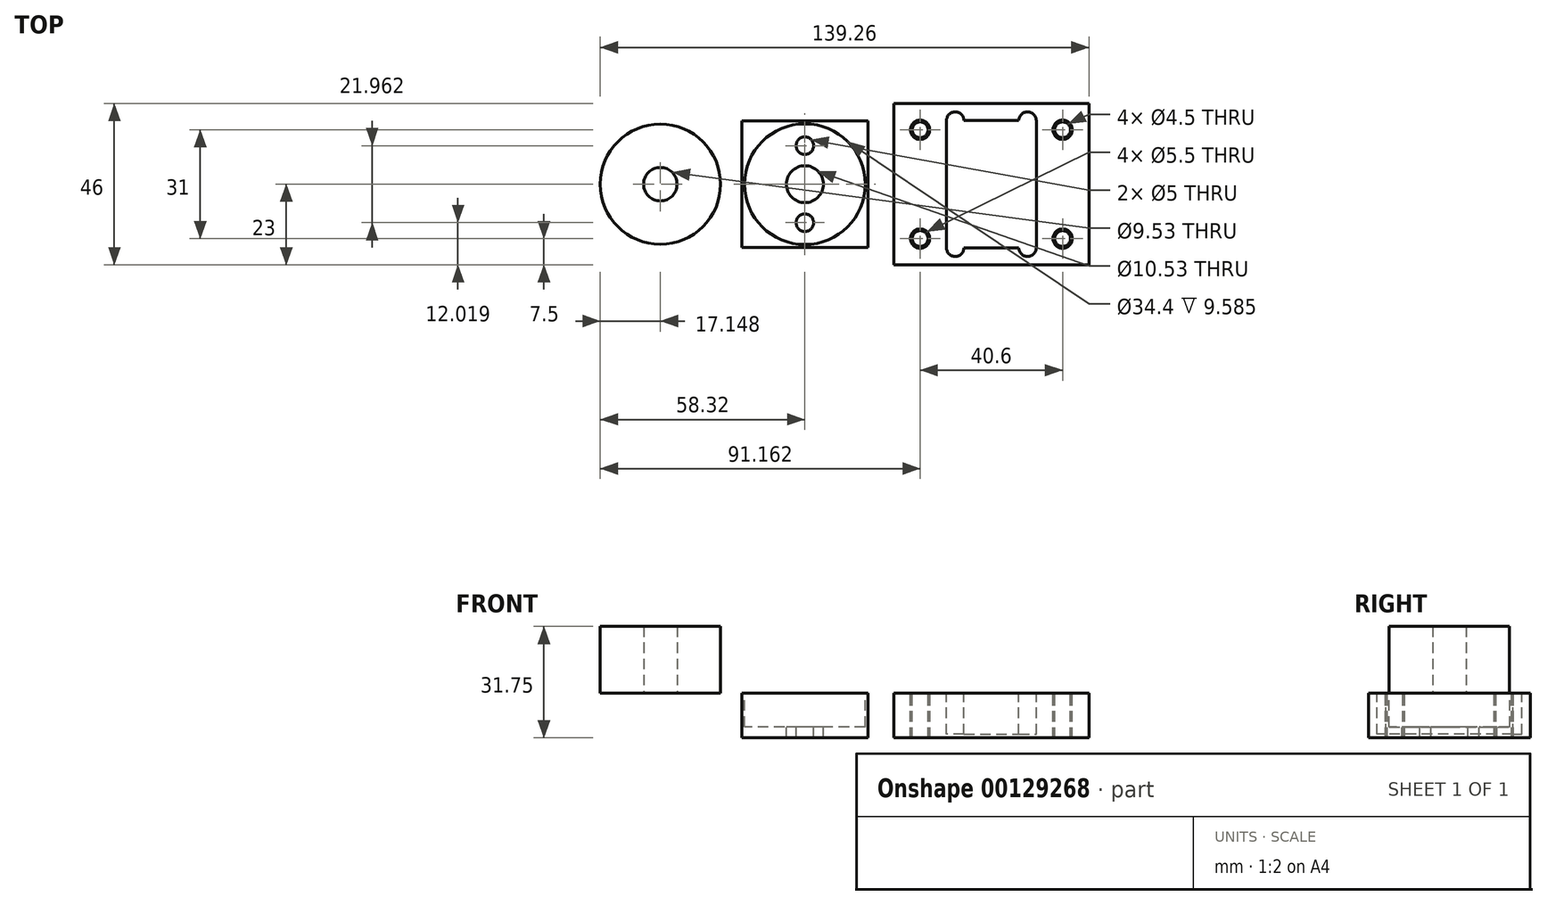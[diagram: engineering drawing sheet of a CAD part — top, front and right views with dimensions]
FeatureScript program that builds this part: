
annotation { "Feature Type Name" : "Feature", "Feature Type Description" : "" }
export const myFeature = defineFeature(function(context is Context, id is Id, definition is map)
    precondition{}
    {
        {
            var Q0;
            Q0=qCreatedBy(makeId("Top.planeOp"),FACE);
            var sketch = newSketch(context, id + "F0", { "sketchPlane" : qUnion([Q0])});
            skLineSegment(sketch, "E0.bottom", {"start": v(-18, 18) * mm, "end": v(18, 18) * mm});
            skLineSegment(sketch, "E0.top", {"start": v(-18, -18) * mm, "end": v(18, -18) * mm});
            skLineSegment(sketch, "E0.left", {"start": v(-18, 18) * mm, "end": v(-18, -18) * mm});
            skLineSegment(sketch, "E0.right", {"start": v(18, 18) * mm, "end": v(18, -18) * mm});
            skLineSegment(sketch, "E1", {"start": v(-18, 0) * mm, "end": v(18, 0) * mm, "construction": true});
            skLineSegment(sketch, "E2", {"start": v(0, 18) * mm, "end": v(0, -18) * mm, "construction": true});
            skPoint(sketch, "E3", {"position": v(0, 0) * mm});
            skCircle(sketch, "E4", {"center": v(0, 0) * mm, "radius": 17.2 * mm});
            skCircle(sketch, "E5", {"center": v(0, 0) * mm, "radius": 4.76 * mm, "construction": true});
            skPoint(sketch, "E6", {"position": v(-4.76, 0) * mm});
            skPoint(sketch, "E7", {"position": v(-17.2, 0) * mm});
            skLineSegment(sketch, "E8", {"start": v(-17.2, 0) * mm, "end": v(-4.76, 0) * mm});
            skCircle(sketch, "E9", {"center": v(0, 0) * mm, "radius": 10.98 * mm, "construction": true});
            skPoint(sketch, "E10", {"position": v(-10.98, 0) * mm});
            skCircle(sketch, "E11", {"center": v(0, 0) * mm, "radius": 5.26 * mm});
            skCircle(sketch, "E12", {"center": v(0, 10.98) * mm, "radius": 2.5 * mm});
            skCircle(sketch, "E13", {"center": v(-10.98, 0) * mm, "radius": 2.5 * mm, "construction": true});
            skCircle(sketch, "E14", {"center": v(0, -10.98) * mm, "radius": 2.5 * mm});
            skCircle(sketch, "E15", {"center": v(10.98, 0) * mm, "radius": 2.5 * mm, "construction": true});
            skPoint(sketch, "E16", {"position": v(0, 17.2) * mm});
            skPoint(sketch, "E17", {"position": v(17.2, 0) * mm});
            skPoint(sketch, "E18", {"position": v(-13.48, 0) * mm});
            skSolve(sketch);
        }
        {
            var Q0;
            Q0=makeQuery(id+"F0.imprint","IMPRINT",FACE,{"disambiguationData":[TD([[makeQuery(id+"F0.imprint","IMPRINT",EDGE,{"derivedFrom":sQuery(id+"F0.wireOp",EDGE,"E0.bottom")}),-1.0]])]});
            var Q1;
            Q1=makeQuery(id+"F0.imprint","IMPRINT",FACE,{"disambiguationData":[TD([[makeQuery(id+"F0.imprint","IMPRINT",EDGE,{"derivedFrom":sQuery(id+"F0.wireOp",EDGE,"E4")}),1.0]])]});
            extrude(context, id + "F1", {"entities" : qUnion([Q0, Q1]), "oppositeDirection" : true, "depth" : 25.4 * mm / 2});
        }
        {
            var Q0;
            Q0=makeQuery(id+"F0.imprint","IMPRINT",FACE,{"disambiguationData":[TD([[makeQuery(id+"F0.imprint","IMPRINT",EDGE,{"derivedFrom":sQuery(id+"F0.wireOp",EDGE,"E4")}),1.0]])]});
            extrude(context, id + "F2", {"entities" : qUnion([Q0]), "operationType" : NewBodyOperationType.REMOVE, "oppositeDirection" : true, "depth" : (19.17 / 2) * mm});
        }
        {
            var Q0;
            Q0=qCreatedBy(makeId("Top.planeOp"),FACE);
            var sketch = newSketch(context, id + "F3", { "sketchPlane" : qUnion([Q0])});
            skLineSegment(sketch, "E19", {"start": v(18, 18) * mm, "end": v(40.44, 18) * mm, "construction": true});
            skLineSegment(sketch, "E20", {"start": v(40.44, -18) * mm, "end": v(18, -18) * mm, "construction": true});
            skPoint(sketch, "E21", {"position": v(0, 5.26) * mm});
            skPoint(sketch, "E22", {"position": v(0, -5.26) * mm});
            skLineSegment(sketch, "E23.bottom", {"start": v(40.44, 18) * mm, "end": v(65.84, 18) * mm, "construction": true});
            skLineSegment(sketch, "E23.top", {"start": v(40.44, -18) * mm, "end": v(65.84, -18) * mm, "construction": true});
            skLineSegment(sketch, "E23.left", {"start": v(40.44, 18) * mm, "end": v(40.44, -18) * mm, "construction": true});
            skLineSegment(sketch, "E23.right", {"start": v(65.84, 18) * mm, "end": v(65.84, -18) * mm, "construction": true});
            skLineSegment(sketch, "E24.0", {"start": v(40.34, 18.1) * mm, "end": v(45.34, 18.1) * mm, "construction": true});
            skLineSegment(sketch, "E24.1", {"start": v(40.34, 18.1) * mm, "end": v(40.34, -18.1) * mm});
            skLineSegment(sketch, "E24.2", {"start": v(40.34, -18.1) * mm, "end": v(45.34, -18.1) * mm, "construction": true});
            skLineSegment(sketch, "E24.3", {"start": v(65.94, 18.1) * mm, "end": v(65.94, -18.1) * mm});
            skLineSegment(sketch, "E25.0", {"start": v(25.34, 23) * mm, "end": v(80.94, 23) * mm});
            skLineSegment(sketch, "E25.2", {"start": v(25.34, -23) * mm, "end": v(80.94, -23) * mm});
            skLineSegment(sketch, "E26.0", {"start": v(25.34, 23) * mm, "end": v(25.34, -23) * mm});
            skLineSegment(sketch, "E27.0", {"start": v(80.94, 23) * mm, "end": v(80.94, -23) * mm});
            skArc(sketch, "E28", {"start": v(65.94, 18.1) * mm, "mid": v(63.44, 20.6) * mm, "end": v(60.94, 18.1) * mm});
            skArc(sketch, "E29", {"start": v(45.34, 18.1) * mm, "mid": v(42.84, 20.6) * mm, "end": v(40.34, 18.1) * mm});
            skArc(sketch, "E30", {"start": v(40.34, -18.1) * mm, "mid": v(42.84, -20.6) * mm, "end": v(45.34, -18.1) * mm});
            skArc(sketch, "E31", {"start": v(60.94, -18.1) * mm, "mid": v(63.44, -20.6) * mm, "end": v(65.94, -18.1) * mm});
            skLineSegment(sketch, "E32", {"start": v(0, 5.26) * mm, "end": v(80.94, 5.26) * mm, "construction": true});
            skLineSegment(sketch, "E33", {"start": v(0, -5.26) * mm, "end": v(80.94, -5.26) * mm, "construction": true});
            skLineSegment(sketch, "E34", {"start": v(45.34, 18.1) * mm, "end": v(60.94, 18.1) * mm});
            skLineSegment(sketch, "E35", {"start": v(60.94, 18.1) * mm, "end": v(65.94, 18.1) * mm, "construction": true});
            skLineSegment(sketch, "E36", {"start": v(60.94, -18.1) * mm, "end": v(65.94, -18.1) * mm, "construction": true});
            skLineSegment(sketch, "E37", {"start": v(45.34, -18.1) * mm, "end": v(60.94, -18.1) * mm});
            skPoint(sketch, "E38", {"position": v(0, -10.98) * mm});
            skPoint(sketch, "E39", {"position": v(0, 10.98) * mm});
            skLineSegment(sketch, "E40", {"start": v(0, 10.98) * mm, "end": v(80.94, 10.98) * mm, "construction": true});
            skLineSegment(sketch, "E41", {"start": v(0, -10.98) * mm, "end": v(80.94, -10.98) * mm, "construction": true});
            skLineSegment(sketch, "E42", {"start": v(32.84, 23) * mm, "end": v(32.84, -23) * mm, "construction": true});
            skLineSegment(sketch, "E43", {"start": v(73.44, 23) * mm, "end": v(73.44, -23) * mm, "construction": true});
            skLineSegment(sketch, "E44", {"start": v(25.34, 15.5) * mm, "end": v(80.94, 15.5) * mm, "construction": true});
            skLineSegment(sketch, "E45", {"start": v(25.34, -15.5) * mm, "end": v(80.94, -15.5) * mm, "construction": true});
            skCircle(sketch, "E46", {"center": v(32.84, 15.5) * mm, "radius": 2.25 * mm});
            skCircle(sketch, "E47", {"center": v(32.84, -15.5) * mm, "radius": 2.25 * mm});
            skCircle(sketch, "E48", {"center": v(73.44, 15.5) * mm, "radius": 2.25 * mm});
            skCircle(sketch, "E49", {"center": v(73.44, -15.5) * mm, "radius": 2.25 * mm});
            skCircle(sketch, "E50", {"center": v(32.84, 15.5) * mm, "radius": 2.75 * mm});
            skCircle(sketch, "E51", {"center": v(32.84, -15.5) * mm, "radius": 2.75 * mm});
            skCircle(sketch, "E52", {"center": v(73.44, 15.5) * mm, "radius": 2.75 * mm});
            skCircle(sketch, "E53", {"center": v(73.44, -15.5) * mm, "radius": 2.75 * mm});
            skSolve(sketch);
        }
        {
            var Q0;
            Q0=makeQuery(id+"F3.imprint","IMPRINT",FACE,{"disambiguationData":[TD([[makeQuery(id+"F3.imprint","IMPRINT",EDGE,{"derivedFrom":sQuery(id+"F3.wireOp",EDGE,"E24.1")}),1.0]])]});
            var Q1;
            Q1=makeQuery(id+"F3.imprint","IMPRINT",FACE,{"disambiguationData":[TD([[makeQuery(id+"F3.imprint","IMPRINT",EDGE,{"derivedFrom":sQuery(id+"F3.wireOp",EDGE,"E24.1")}),-1.0]])]});
            var Q2;
            Q2=makeQuery(id+"F3.imprint","IMPRINT",FACE,{"disambiguationData":[TD([[makeQuery(id+"F3.imprint","IMPRINT",EDGE,{"derivedFrom":sQuery(id+"F3.wireOp",EDGE,"E46")}),-1.0]])]});
            var Q3;
            Q3=makeQuery(id+"F3.imprint","IMPRINT",FACE,{"disambiguationData":[TD([[makeQuery(id+"F3.imprint","IMPRINT",EDGE,{"derivedFrom":sQuery(id+"F3.wireOp",EDGE,"E47")}),-1.0]])]});
            var Q4;
            Q4=makeQuery(id+"F3.imprint","IMPRINT",FACE,{"disambiguationData":[TD([[makeQuery(id+"F3.imprint","IMPRINT",EDGE,{"derivedFrom":sQuery(id+"F3.wireOp",EDGE,"E49")}),-1.0]])]});
            var Q5;
            Q5=makeQuery(id+"F3.imprint","IMPRINT",FACE,{"disambiguationData":[TD([[makeQuery(id+"F3.imprint","IMPRINT",EDGE,{"derivedFrom":sQuery(id+"F3.wireOp",EDGE,"E48")}),-1.0]])]});
            extrude(context, id + "F4", {"entities" : qUnion([Q0, Q1, Q2, Q3, Q4, Q5]), "oppositeDirection" : true, "depth" : 25.4 * mm / 2});
        }
        {
            var Q0;
            Q0=makeQuery(id+"F3.imprint","IMPRINT",FACE,{"disambiguationData":[TD([[makeQuery(id+"F3.imprint","IMPRINT",EDGE,{"derivedFrom":sQuery(id+"F3.wireOp",EDGE,"E24.1")}),1.0]])]});
            extrude(context, id + "F5", {"entities" : qUnion([Q0]), "operationType" : NewBodyOperationType.REMOVE, "oppositeDirection" : true, "depth" : 11.7 * mm});
        }
        {
            var Q0;
            Q0=qCreatedBy(makeId("Top.planeOp"),FACE);
            var sketch = newSketch(context, id + "F6", { "sketchPlane" : qUnion([Q0])});
            skCircle(sketch, "E54", {"center": v(-41.17, 0) * mm, "radius": 17.15 * mm});
            skCircle(sketch, "E55", {"center": v(-41.17, 0) * mm, "radius": 4.76 * mm});
            skSolve(sketch);
        }
        {
            var Q0;
            Q0=makeQuery(id+"F6.imprint","IMPRINT",FACE,{"disambiguationData":[TD([[makeQuery(id+"F6.imprint","IMPRINT",EDGE,{"derivedFrom":sQuery(id+"F6.wireOp",EDGE,"E54")}),1.0]])]});
            extrude(context, id + "F7", {"entities" : qUnion([Q0]), "depth" : 19.05 * mm});
        }
        {
            var Q0;
            Q0=makeQuery(id+"F3.imprint","IMPRINT",FACE,{"disambiguationData":[TD([[makeQuery(id+"F3.imprint","IMPRINT",EDGE,{"derivedFrom":sQuery(id+"F3.wireOp",EDGE,"E24.1")}),-1.0]])]});
            var Q1;
            Q1=makeQuery(id+"F3.imprint","IMPRINT",FACE,{"disambiguationData":[TD([[makeQuery(id+"F3.imprint","IMPRINT",EDGE,{"derivedFrom":sQuery(id+"F3.wireOp",EDGE,"E24.1")}),1.0]])]});
            extrude(context, id + "F8", {"entities" : qUnion([Q0, Q1]), "oppositeDirection" : true, "depth" : 25.4 * mm / 2});
        }
        {
            var Q0;
            Q0=makeQuery(id+"F3.imprint","IMPRINT",FACE,{"disambiguationData":[TD([[makeQuery(id+"F3.imprint","IMPRINT",EDGE,{"derivedFrom":sQuery(id+"F3.wireOp",EDGE,"E24.1")}),1.0]])]});
            extrude(context, id + "F9", {"entities" : qUnion([Q0]), "operationType" : NewBodyOperationType.REMOVE, "oppositeDirection" : true, "depth" : 1 / 50.8 * mm - 7.4 * mm});
        }
    });
